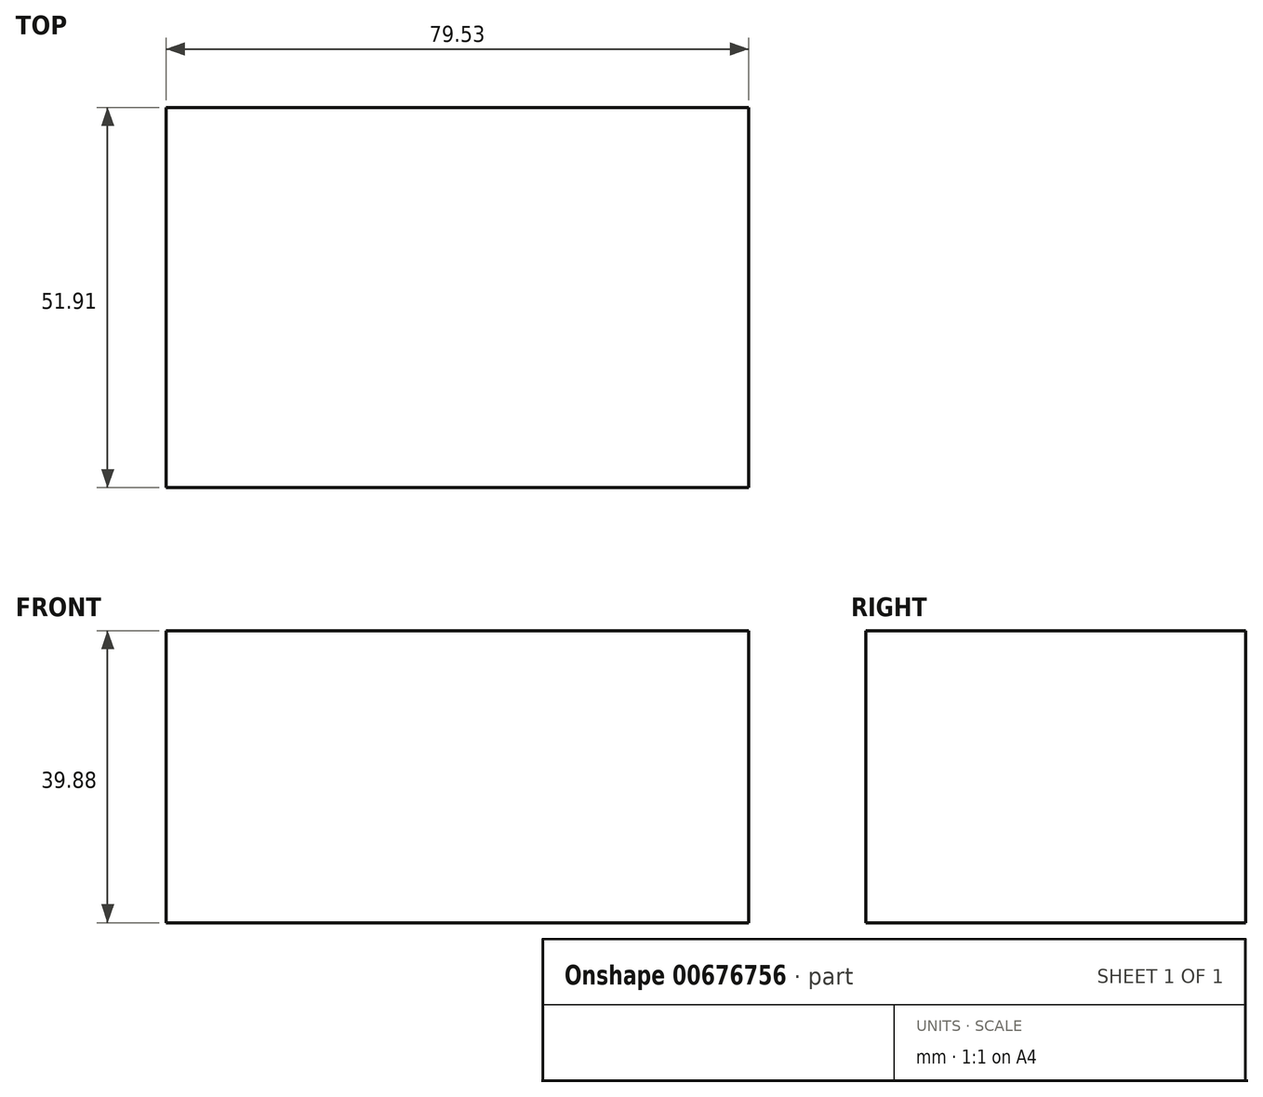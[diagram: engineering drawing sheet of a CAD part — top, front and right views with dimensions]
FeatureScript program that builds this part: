
annotation { "Feature Type Name" : "Feature", "Feature Type Description" : "" }
export const myFeature = defineFeature(function(context is Context, id is Id, definition is map)
    precondition{}
    {
        {
            var Q0;
            Q0=qCreatedBy(makeId("Top.planeOp"),FACE);
            var sketch = newSketch(context, id + "F0", { "sketchPlane" : qUnion([Q0])});
            skLineSegment(sketch, "E0.bottom", {"start": v(0, 0) * mm, "end": v(-79.53, 0) * mm});
            skLineSegment(sketch, "E0.top", {"start": v(0, 51.91) * mm, "end": v(-79.53, 51.91) * mm});
            skLineSegment(sketch, "E0.left", {"start": v(0, 0) * mm, "end": v(0, 51.91) * mm});
            skLineSegment(sketch, "E0.right", {"start": v(-79.53, 0) * mm, "end": v(-79.53, 51.91) * mm});
            skSolve(sketch);
        }
        {
            var Q0;
            Q0=makeQuery(id+"F0.imprint","IMPRINT",FACE,{"disambiguationData":[TD([[makeQuery(id+"F0.imprint","IMPRINT",EDGE,{"derivedFrom":sQuery(id+"F0.wireOp",EDGE,"E0.bottom")}),-1.0]])]});
            extrude(context, id + "F1", {"entities" : qUnion([Q0]), "depth" : 39.88 * mm, "offsetDistance" : 25.4 * mm});
        }
    });
